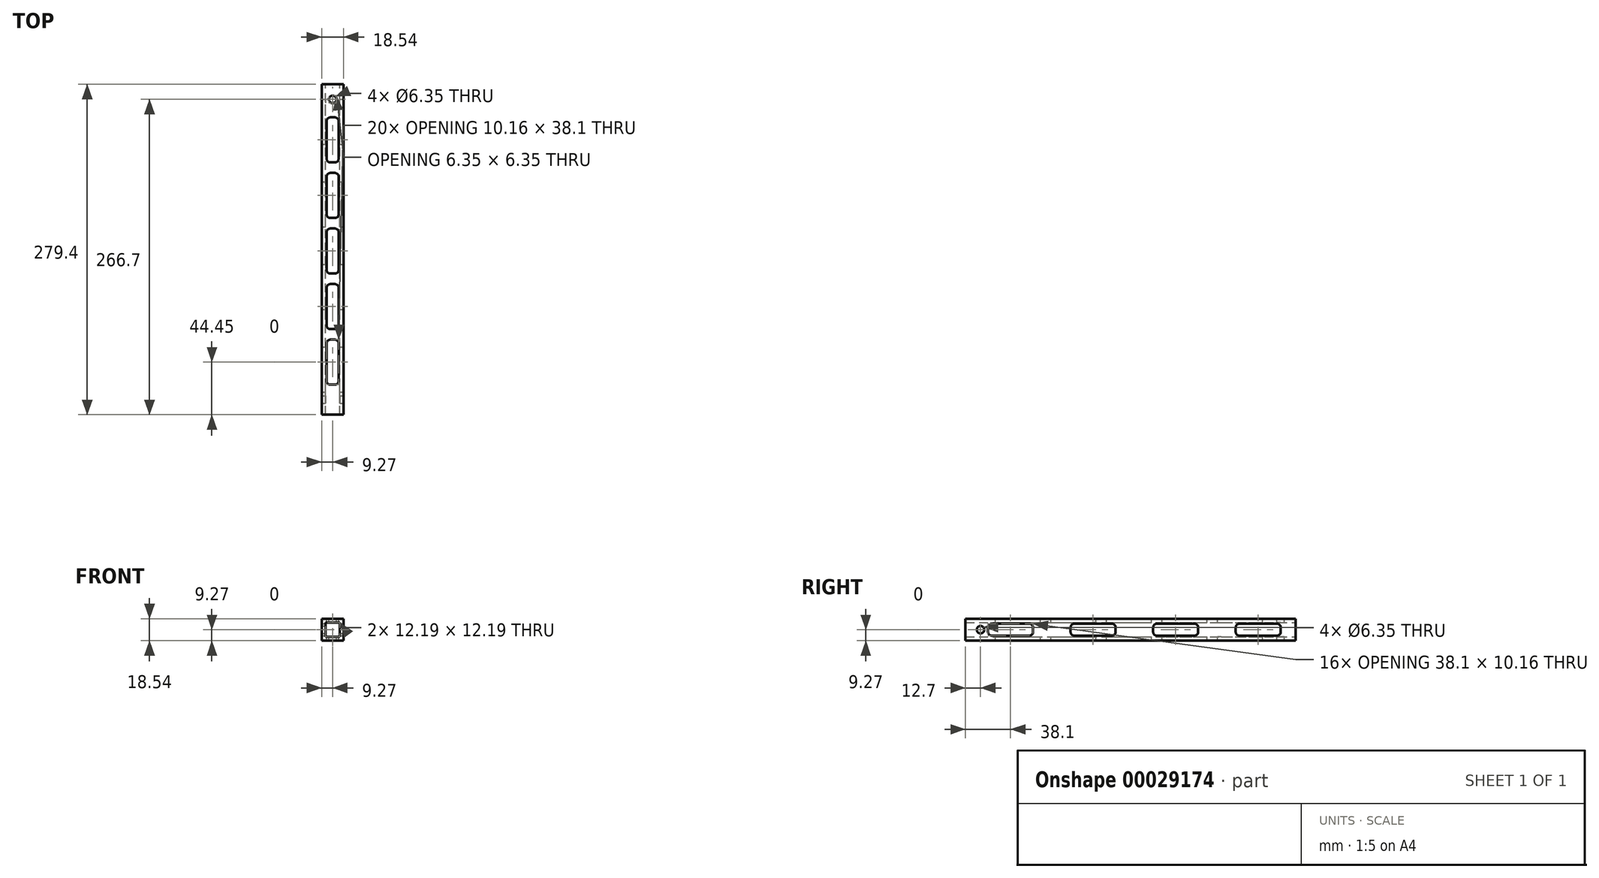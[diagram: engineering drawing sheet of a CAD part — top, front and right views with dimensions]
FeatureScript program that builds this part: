
annotation { "Feature Type Name" : "Feature", "Feature Type Description" : "" }
export const myFeature = defineFeature(function(context is Context, id is Id, definition is map)
    precondition{}
    {
        {
            var Q0;
            Q0=qCreatedBy(makeId("Front.planeOp"),FACE);
            var sketch = newSketch(context, id + "F0", { "sketchPlane" : qUnion([Q0])});
            skLineSegment(sketch, "E0.rect.bottom", {"start": v(9.27, 9.27) * mm, "end": v(-9.27, 9.27) * mm});
            skLineSegment(sketch, "E0.rect.top", {"start": v(9.27, -9.27) * mm, "end": v(-9.27, -9.27) * mm});
            skLineSegment(sketch, "E0.rect.left", {"start": v(9.27, 9.27) * mm, "end": v(9.27, -9.27) * mm});
            skLineSegment(sketch, "E0.rect.right", {"start": v(-9.27, 9.27) * mm, "end": v(-9.27, -9.27) * mm});
            skPoint(sketch, "E0.rect.middle", {"position": v(0, 0) * mm});
            skLineSegment(sketch, "E1.rect.bottom", {"start": v(6.1, 6.1) * mm, "end": v(-6.1, 6.1) * mm});
            skLineSegment(sketch, "E1.rect.top", {"start": v(6.1, -6.1) * mm, "end": v(-6.1, -6.1) * mm});
            skLineSegment(sketch, "E1.rect.left", {"start": v(6.1, 6.1) * mm, "end": v(6.1, -6.1) * mm});
            skLineSegment(sketch, "E1.rect.right", {"start": v(-6.1, 6.1) * mm, "end": v(-6.1, -6.1) * mm});
            skSolve(sketch);
        }
        {
            var Q0;
            Q0=makeQuery(id+"F0.imprint","IMPRINT",FACE,{"disambiguationData":[TD([[makeQuery(id+"F0.imprint","IMPRINT",EDGE,{"derivedFrom":sQuery(id+"F0.wireOp",EDGE,"E0.rect.bottom")}),1.0]])]});
            extrude(context, id + "F1", {"entities" : qUnion([Q0]), "depth" : 279.4 * mm});
        }
        {
            var Q0;
            Q0=makeQuery(id+"F1.opExtrude","SWEPT_FACE",FACE,{"disambiguationData":[OSD([sQuery(id+"F0.wireOp",EDGE,"E0.rect.bottom")])]});
            var sketch = newSketch(context, id + "F2", { "sketchPlane" : qUnion([Q0])});
            skLineSegment(sketch, "E2", {"start": v(0, -279.4) * mm, "end": v(0, -254) * mm});
            skCircle(sketch, "E3", {"center": v(0, -12.7) * mm, "radius": 3.18 * mm});
            skLineSegment(sketch, "E4.trimOffspring", {"start": v(0, -9.52) * mm, "end": v(0, 0) * mm});
            skLineSegment(sketch, "E5.rect.bottom", {"start": v(1.9, -215.9) * mm, "end": v(-1.9, -215.9) * mm});
            skLineSegment(sketch, "E5.rect.top", {"start": v(1.9, -254) * mm, "end": v(-1.9, -254) * mm});
            skLineSegment(sketch, "E5.rect.left", {"start": v(5.08, -219.08) * mm, "end": v(5.08, -250.83) * mm});
            skLineSegment(sketch, "E5.rect.right", {"start": v(-5.08, -219.08) * mm, "end": v(-5.08, -250.83) * mm});
            skPoint(sketch, "E5.rect.middle", {"position": v(0, -234.95) * mm});
            skPoint(sketch, "E6.visualSharp", {"position": v(-5.08, -215.9) * mm});
            skArc(sketch, "E6.filletArc", {"start": v(-1.9, -215.9) * mm, "mid": v(-4.15, -216.83) * mm, "end": v(-5.08, -219.08) * mm});
            skPoint(sketch, "E7.visualSharp", {"position": v(5.08, -215.9) * mm});
            skArc(sketch, "E7.filletArc", {"start": v(5.08, -219.08) * mm, "mid": v(4.15, -216.83) * mm, "end": v(1.9, -215.9) * mm});
            skPoint(sketch, "E8.visualSharp", {"position": v(5.08, -254) * mm});
            skArc(sketch, "E8.filletArc", {"start": v(1.9, -254) * mm, "mid": v(4.15, -253.07) * mm, "end": v(5.08, -250.83) * mm});
            skPoint(sketch, "E9.visualSharp", {"position": v(-5.08, -254) * mm});
            skArc(sketch, "E9.filletArc", {"start": v(-5.08, -250.83) * mm, "mid": v(-4.15, -253.07) * mm, "end": v(-1.9, -254) * mm});
            skLineSegment(sketch, "E10.trimOffspring", {"start": v(0, -215.9) * mm, "end": v(0, -15.87) * mm});
            skLineSegment(sketch, "E11.0.1.0", {"start": v(1.9, -168.91) * mm, "end": v(-1.9, -168.91) * mm});
            skArc(sketch, "E11.0.1.1", {"start": v(-1.9, -168.91) * mm, "mid": v(-4.15, -169.84) * mm, "end": v(-5.08, -172.09) * mm});
            skArc(sketch, "E11.0.1.2", {"start": v(5.08, -172.09) * mm, "mid": v(4.15, -169.84) * mm, "end": v(1.9, -168.91) * mm});
            skLineSegment(sketch, "E11.0.1.3", {"start": v(5.08, -172.09) * mm, "end": v(5.08, -203.84) * mm});
            skLineSegment(sketch, "E11.0.1.4", {"start": v(-5.08, -172.09) * mm, "end": v(-5.08, -203.84) * mm});
            skArc(sketch, "E11.0.1.5", {"start": v(-5.08, -203.84) * mm, "mid": v(-4.15, -206.08) * mm, "end": v(-1.9, -207.01) * mm});
            skLineSegment(sketch, "E11.0.1.6", {"start": v(1.9, -207.01) * mm, "end": v(-1.9, -207.01) * mm});
            skArc(sketch, "E11.0.1.7", {"start": v(1.9, -207.01) * mm, "mid": v(4.15, -206.08) * mm, "end": v(5.08, -203.84) * mm});
            skLineSegment(sketch, "E11.0.2.0", {"start": v(1.9, -121.92) * mm, "end": v(-1.9, -121.92) * mm});
            skArc(sketch, "E11.0.2.1", {"start": v(-1.9, -121.92) * mm, "mid": v(-4.15, -122.85) * mm, "end": v(-5.08, -125.1) * mm});
            skArc(sketch, "E11.0.2.2", {"start": v(5.08, -125.1) * mm, "mid": v(4.15, -122.85) * mm, "end": v(1.9, -121.92) * mm});
            skLineSegment(sketch, "E11.0.2.3", {"start": v(5.08, -125.1) * mm, "end": v(5.08, -156.85) * mm});
            skLineSegment(sketch, "E11.0.2.4", {"start": v(-5.08, -125.1) * mm, "end": v(-5.08, -156.85) * mm});
            skArc(sketch, "E11.0.2.5", {"start": v(-5.08, -156.85) * mm, "mid": v(-4.15, -159.1) * mm, "end": v(-1.9, -160.02) * mm});
            skLineSegment(sketch, "E11.0.2.6", {"start": v(1.9, -160.02) * mm, "end": v(-1.9, -160.02) * mm});
            skArc(sketch, "E11.0.2.7", {"start": v(1.9, -160.02) * mm, "mid": v(4.15, -159.1) * mm, "end": v(5.08, -156.85) * mm});
            skLineSegment(sketch, "E11.0.3.0", {"start": v(1.9, -74.93) * mm, "end": v(-1.9, -74.93) * mm});
            skArc(sketch, "E11.0.3.1", {"start": v(-1.9, -74.93) * mm, "mid": v(-4.15, -75.86) * mm, "end": v(-5.08, -78.1) * mm});
            skArc(sketch, "E11.0.3.2", {"start": v(5.08, -78.1) * mm, "mid": v(4.15, -75.86) * mm, "end": v(1.9, -74.93) * mm});
            skLineSegment(sketch, "E11.0.3.3", {"start": v(5.08, -78.1) * mm, "end": v(5.08, -109.86) * mm});
            skLineSegment(sketch, "E11.0.3.4", {"start": v(-5.08, -78.1) * mm, "end": v(-5.08, -109.86) * mm});
            skArc(sketch, "E11.0.3.5", {"start": v(-5.08, -109.86) * mm, "mid": v(-4.15, -112.1) * mm, "end": v(-1.9, -113.03) * mm});
            skLineSegment(sketch, "E11.0.3.6", {"start": v(1.9, -113.03) * mm, "end": v(-1.9, -113.03) * mm});
            skArc(sketch, "E11.0.3.7", {"start": v(1.9, -113.03) * mm, "mid": v(4.15, -112.1) * mm, "end": v(5.08, -109.86) * mm});
            skLineSegment(sketch, "E11.0.4.0", {"start": v(1.9, -27.94) * mm, "end": v(-1.9, -27.94) * mm});
            skArc(sketch, "E11.0.4.1", {"start": v(-1.9, -27.94) * mm, "mid": v(-4.15, -28.87) * mm, "end": v(-5.08, -31.12) * mm});
            skArc(sketch, "E11.0.4.2", {"start": v(5.08, -31.12) * mm, "mid": v(4.15, -28.87) * mm, "end": v(1.9, -27.94) * mm});
            skLineSegment(sketch, "E11.0.4.3", {"start": v(5.08, -31.12) * mm, "end": v(5.08, -62.87) * mm});
            skLineSegment(sketch, "E11.0.4.4", {"start": v(-5.08, -31.12) * mm, "end": v(-5.08, -62.87) * mm});
            skArc(sketch, "E11.0.4.5", {"start": v(-5.08, -62.87) * mm, "mid": v(-4.15, -65.11) * mm, "end": v(-1.9, -66.04) * mm});
            skLineSegment(sketch, "E11.0.4.6", {"start": v(1.9, -66.04) * mm, "end": v(-1.9, -66.04) * mm});
            skArc(sketch, "E11.0.4.7", {"start": v(1.9, -66.04) * mm, "mid": v(4.15, -65.11) * mm, "end": v(5.08, -62.87) * mm});
            skLineSegment(sketch, "E11.direction1", {"start": v(-1.9, -215.9) * mm, "end": v(23.5, -215.9) * mm, "construction": true});
            skLineSegment(sketch, "E11.direction2", {"start": v(-1.9, -215.9) * mm, "end": v(-1.9, -168.91) * mm, "construction": true});
            skSolve(sketch);
        }
        {
            var Q0;
            {var subQ0=sQuery(id+"F2.wireOp",EDGE,"E3");var subQ2=makeQuery(id+"F2.imprint","INTERSECT",VERTEX,{"derivedFrom":[sQuery(id+"F2.wireOp",EDGE,"E2"),subQ0]});Q0=makeQuery(id+"F2.imprint","IMPRINT",FACE,{"disambiguationData":[TD([[makeQuery(id+"F2.imprint","IMPRINT",EDGE,{"disambiguationData":[TD([[subQ2,1.0]])],"derivedFrom":subQ0}),1.0]])]});}
            extrude(context, id + "F3", {"entities" : qUnion([Q0]), "operationType" : NewBodyOperationType.REMOVE, "oppositeDirection" : true, "depth" : 25.4 * mm});
        }
        {
            var Q0;
            Q0=makeQuery(id+"F1.opExtrude","SWEPT_FACE",FACE,{"disambiguationData":[OSD([sQuery(id+"F0.wireOp",EDGE,"E0.rect.left")])]});
            var sketch = newSketch(context, id + "F4", { "sketchPlane" : qUnion([Q0])});
            skLineSegment(sketch, "E12", {"start": v(-279.4, 0) * mm, "end": v(-269.88, 0) * mm});
            skCircle(sketch, "E13", {"center": v(-266.7, 0) * mm, "radius": 3.18 * mm});
            skLineSegment(sketch, "E14.trimOffspring", {"start": v(-263.53, 0) * mm, "end": v(0, 0) * mm});
            skLineSegment(sketch, "E15.rect.bottom", {"start": v(-47.63, -5.08) * mm, "end": v(-15.88, -5.08) * mm});
            skLineSegment(sketch, "E15.rect.top", {"start": v(-47.63, 5.08) * mm, "end": v(-15.88, 5.08) * mm});
            skLineSegment(sketch, "E15.rect.left", {"start": v(-50.8, -1.9) * mm, "end": v(-50.8, 1.9) * mm});
            skLineSegment(sketch, "E15.rect.right", {"start": v(-12.7, -1.9) * mm, "end": v(-12.7, 1.9) * mm});
            skPoint(sketch, "E15.rect.middle", {"position": v(-31.75, 0) * mm});
            skPoint(sketch, "E16.visualSharp", {"position": v(-50.8, 5.08) * mm});
            skArc(sketch, "E16.filletArc", {"start": v(-47.63, 5.08) * mm, "mid": v(-49.87, 4.15) * mm, "end": v(-50.8, 1.9) * mm});
            skPoint(sketch, "E17.visualSharp", {"position": v(-50.8, -5.08) * mm});
            skArc(sketch, "E17.filletArc", {"start": v(-50.8, -1.9) * mm, "mid": v(-49.87, -4.15) * mm, "end": v(-47.63, -5.08) * mm});
            skPoint(sketch, "E18.visualSharp", {"position": v(-12.7, -5.08) * mm});
            skArc(sketch, "E18.filletArc", {"start": v(-15.88, -5.08) * mm, "mid": v(-13.63, -4.15) * mm, "end": v(-12.7, -1.9) * mm});
            skPoint(sketch, "E19.visualSharp", {"position": v(-12.7, 5.08) * mm});
            skArc(sketch, "E19.filletArc", {"start": v(-12.7, 1.9) * mm, "mid": v(-13.63, 4.15) * mm, "end": v(-15.88, 5.08) * mm});
            skLineSegment(sketch, "E20.1.0.0", {"start": v(-120.65, -1.9) * mm, "end": v(-120.65, 1.9) * mm});
            skArc(sketch, "E20.1.0.1", {"start": v(-117.47, 5.08) * mm, "mid": v(-119.72, 4.15) * mm, "end": v(-120.65, 1.9) * mm});
            skArc(sketch, "E20.1.0.2", {"start": v(-120.65, -1.9) * mm, "mid": v(-119.72, -4.15) * mm, "end": v(-117.47, -5.08) * mm});
            skLineSegment(sketch, "E20.1.0.3", {"start": v(-117.47, -5.08) * mm, "end": v(-85.72, -5.08) * mm});
            skLineSegment(sketch, "E20.1.0.4", {"start": v(-117.47, 5.08) * mm, "end": v(-85.72, 5.08) * mm});
            skArc(sketch, "E20.1.0.5", {"start": v(-82.55, 1.9) * mm, "mid": v(-83.48, 4.15) * mm, "end": v(-85.72, 5.08) * mm});
            skLineSegment(sketch, "E20.1.0.6", {"start": v(-82.55, -1.9) * mm, "end": v(-82.55, 1.9) * mm});
            skArc(sketch, "E20.1.0.7", {"start": v(-85.72, -5.08) * mm, "mid": v(-83.48, -4.15) * mm, "end": v(-82.55, -1.9) * mm});
            skLineSegment(sketch, "E20.2.0.0", {"start": v(-190.5, -1.9) * mm, "end": v(-190.5, 1.9) * mm});
            skArc(sketch, "E20.2.0.1", {"start": v(-187.32, 5.08) * mm, "mid": v(-189.57, 4.15) * mm, "end": v(-190.5, 1.9) * mm});
            skArc(sketch, "E20.2.0.2", {"start": v(-190.5, -1.9) * mm, "mid": v(-189.57, -4.15) * mm, "end": v(-187.32, -5.08) * mm});
            skLineSegment(sketch, "E20.2.0.3", {"start": v(-187.32, -5.08) * mm, "end": v(-155.57, -5.08) * mm});
            skLineSegment(sketch, "E20.2.0.4", {"start": v(-187.32, 5.08) * mm, "end": v(-155.57, 5.08) * mm});
            skArc(sketch, "E20.2.0.5", {"start": v(-152.4, 1.9) * mm, "mid": v(-153.33, 4.15) * mm, "end": v(-155.57, 5.08) * mm});
            skLineSegment(sketch, "E20.2.0.6", {"start": v(-152.4, -1.9) * mm, "end": v(-152.4, 1.9) * mm});
            skArc(sketch, "E20.2.0.7", {"start": v(-155.57, -5.08) * mm, "mid": v(-153.33, -4.15) * mm, "end": v(-152.4, -1.9) * mm});
            skLineSegment(sketch, "E20.3.0.0", {"start": v(-260.35, -1.9) * mm, "end": v(-260.35, 1.9) * mm});
            skArc(sketch, "E20.3.0.1", {"start": v(-257.18, 5.08) * mm, "mid": v(-259.42, 4.15) * mm, "end": v(-260.35, 1.9) * mm});
            skArc(sketch, "E20.3.0.2", {"start": v(-260.35, -1.9) * mm, "mid": v(-259.42, -4.15) * mm, "end": v(-257.18, -5.08) * mm});
            skLineSegment(sketch, "E20.3.0.3", {"start": v(-257.18, -5.08) * mm, "end": v(-225.42, -5.08) * mm});
            skLineSegment(sketch, "E20.3.0.4", {"start": v(-257.18, 5.08) * mm, "end": v(-225.42, 5.08) * mm});
            skArc(sketch, "E20.3.0.5", {"start": v(-222.25, 1.9) * mm, "mid": v(-223.18, 4.15) * mm, "end": v(-225.42, 5.08) * mm});
            skLineSegment(sketch, "E20.3.0.6", {"start": v(-222.25, -1.9) * mm, "end": v(-222.25, 1.9) * mm});
            skArc(sketch, "E20.3.0.7", {"start": v(-225.42, -5.08) * mm, "mid": v(-223.18, -4.15) * mm, "end": v(-222.25, -1.9) * mm});
            skLineSegment(sketch, "E20.direction1", {"start": v(-50.8, -1.9) * mm, "end": v(-120.65, -1.9) * mm, "construction": true});
            skSolve(sketch);
        }
        {
            var Q0;
            Q0 = qSketchRegion(id + "F4", true);
            var Q1;
            {var subQ0=sQuery(id+"F4.wireOp",EDGE,"E13");var subQ2=makeQuery(id+"F4.imprint","INTERSECT",VERTEX,{"derivedFrom":[sQuery(id+"F4.wireOp",EDGE,"E12"),subQ0]});Q1=makeQuery(id+"F4.imprint","IMPRINT",FACE,{"disambiguationData":[TD([[makeQuery(id+"F4.imprint","IMPRINT",EDGE,{"disambiguationData":[TD([[subQ2,1.0]])],"derivedFrom":subQ0}),1.0]])]});}
            extrude(context, id + "F5", {"entities" : qUnion([Q0, Q1]), "operationType" : NewBodyOperationType.REMOVE, "oppositeDirection" : true, "depth" : 25.4 * mm});
        }
        {
            var Q0;
            Q0 = qSketchRegion(id + "F2", true);
            extrude(context, id + "F6", {"entities" : qUnion([Q0]), "operationType" : NewBodyOperationType.REMOVE, "oppositeDirection" : true, "depth" : 25.4 * mm});
        }
    });
